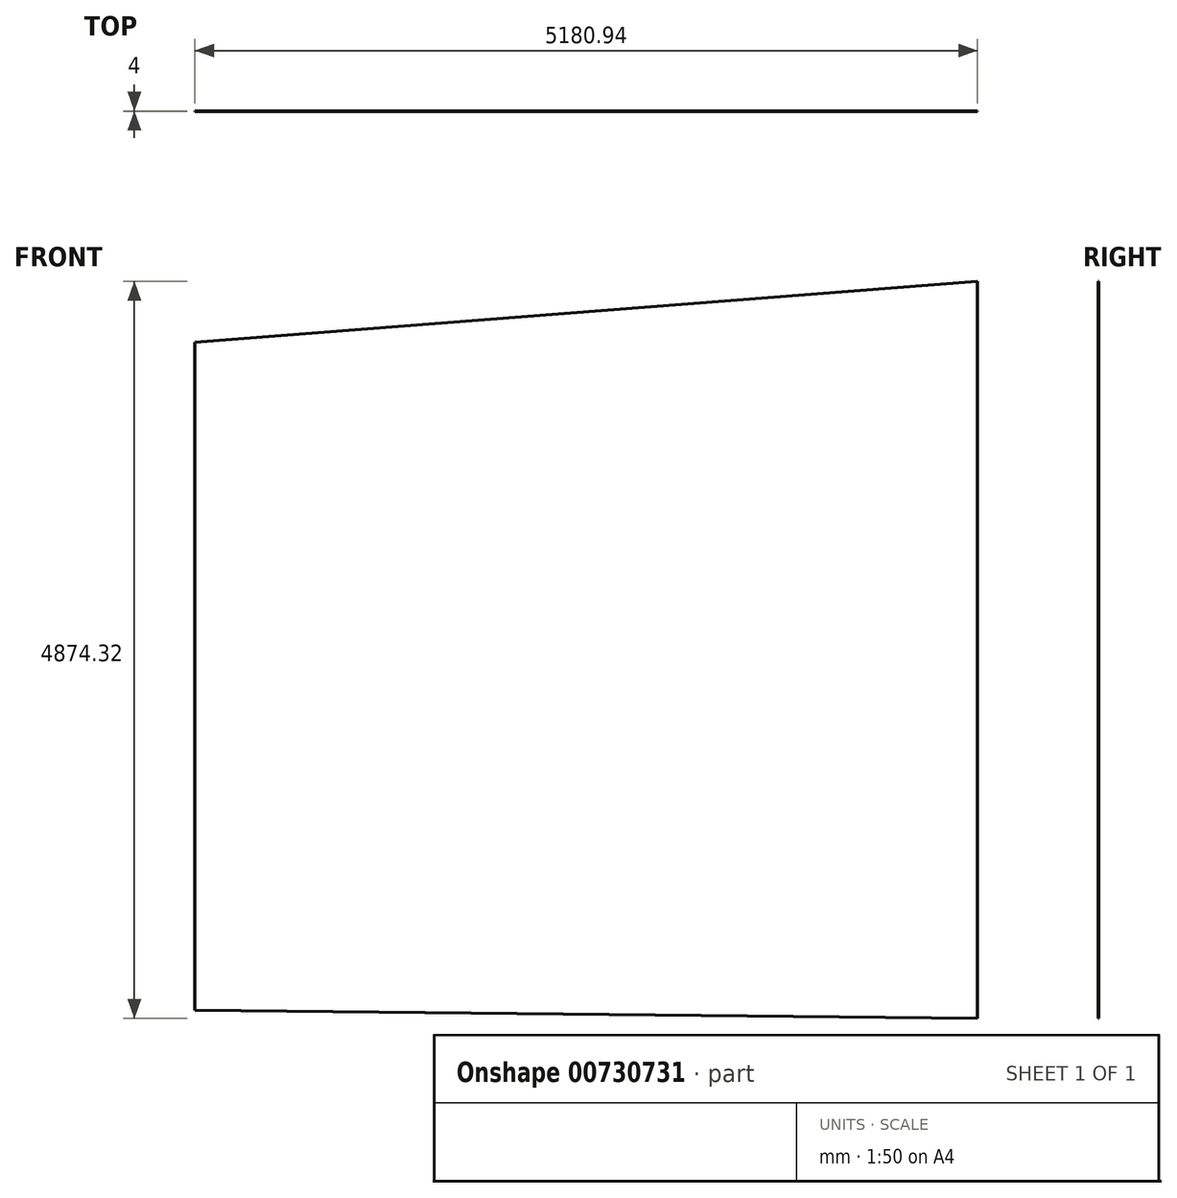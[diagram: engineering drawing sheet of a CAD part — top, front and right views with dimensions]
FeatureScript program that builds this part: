
annotation { "Feature Type Name" : "Feature", "Feature Type Description" : "" }
export const myFeature = defineFeature(function(context is Context, id is Id, definition is map)
    precondition{}
    {
        {
            var Q0;
            Q0=qCreatedBy(makeId("Front.planeOp"),FACE);
            var sketch = newSketch(context, id + "F0", { "sketchPlane" : qUnion([Q0])});
            skLineSegment(sketch, "E0", {"start": v(-2590.47, -2385.26) * mm, "end": v(-2590.47, -175.56) * mm});
            skLineSegment(sketch, "E1", {"start": v(-2590.47, -175.56) * mm, "end": v(-2463.47, -175.56) * mm});
            skLineSegment(sketch, "E2", {"start": v(-2463.47, -175.56) * mm, "end": v(-2590.47, -175.56) * mm});
            skLineSegment(sketch, "E3", {"start": v(-2590.47, -175.56) * mm, "end": v(-2590.47, 2034.16) * mm});
            skLineSegment(sketch, "E4", {"start": v(-2590.47, 2034.16) * mm, "end": v(2590.47, 2437.16) * mm});
            skLineSegment(sketch, "E5", {"start": v(2590.47, 2437.16) * mm, "end": v(2590.47, 0) * mm});
            skLineSegment(sketch, "E6", {"start": v(2590.47, 0) * mm, "end": v(2463.47, 0) * mm});
            skLineSegment(sketch, "E7", {"start": v(2463.47, 0) * mm, "end": v(2590.47, 0) * mm});
            skLineSegment(sketch, "E8", {"start": v(2590.47, 0) * mm, "end": v(2590.47, -2437.16) * mm});
            skLineSegment(sketch, "E9", {"start": v(2590.47, -2437.16) * mm, "end": v(-2590.47, -2385.26) * mm});
            skSolve(sketch);
        }
        {
            var Q0;
            Q0 = qSketchRegion(id + "F0", true);
            var Q1;
            Q1=makeQuery(id+"F0.imprint","IMPRINT",FACE,{"disambiguationData":[TD([[makeQuery(id+"F0.imprint","IMPRINT",EDGE,{"derivedFrom":sQuery(id+"F0.wireOp",EDGE,"E0")}),-1.0]])]});
            extrude(context, id + "F1", {"entities" : qUnion([Q0, Q1]), "depth" : 4 * mm, "offsetDistance" : 25 * mm});
        }
    });
